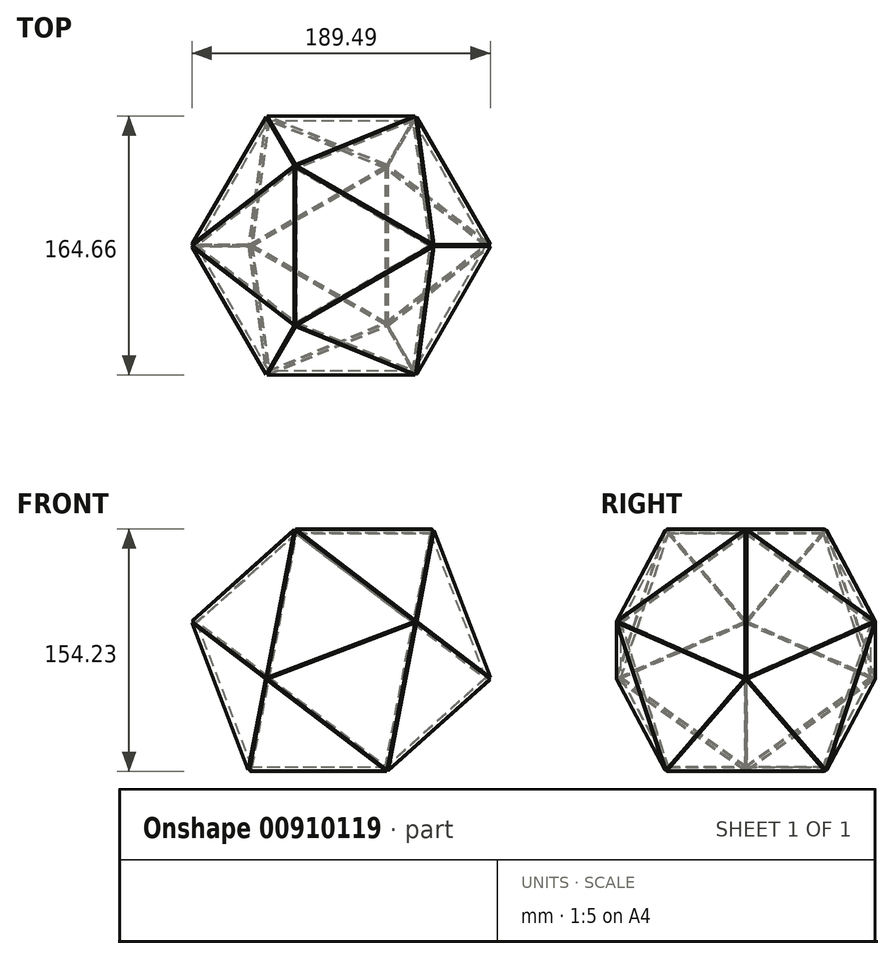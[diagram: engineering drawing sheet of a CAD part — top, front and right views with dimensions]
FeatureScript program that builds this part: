
annotation { "Feature Type Name" : "Feature", "Feature Type Description" : "" }
export const myFeature = defineFeature(function(context is Context, id is Id, definition is map)
    precondition{}
    {
        {
            var Q0;
            Q0=qCreatedBy(makeId("Top.planeOp"),FACE);
            var sketch = newSketch(context, id + "F0", { "sketchPlane" : qUnion([Q0])});
            skCircle(sketch, "E0.cCircle", {"center": v(0, 0) * mm, "radius": 28.87 * mm, "construction": true});
            skLineSegment(sketch, "E0.0", {"start": v(28.87, 50) * mm, "end": v(28.87, -50) * mm});
            skLineSegment(sketch, "E0.1", {"start": v(28.87, -50) * mm, "end": v(-57.74, 0) * mm});
            skLineSegment(sketch, "E0.2", {"start": v(-57.74, 0) * mm, "end": v(28.87, 50) * mm});
            skPoint(sketch, "E0.0.midPoint", {"position": v(28.87, 0) * mm});
            skSolve(sketch);
        }
        {
            var Q0;
            Q0=makeQuery(id+"F0.imprint","IMPRINT",FACE,{"disambiguationData":[TD([[makeQuery(id+"F0.imprint","IMPRINT",EDGE,{"derivedFrom":sQuery(id+"F0.wireOp",EDGE,"E0.0")}),-1.0]])]});
            extrude(context, id + "F1", {"entities" : qUnion([Q0]), "depth" : 3 * mm, "offsetDistance" : 25 * mm});
        }
        {
            var Q0;
            Q0=makeQuery(id+"F1.opExtrude","SWEPT_BODY",BODY,{"disambiguationData":[OSD([sQuery(id+"F0.wireOp",EDGE,"E0.0"),sQuery(id+"F0.wireOp",EDGE,"E0.1"),sQuery(id+"F0.wireOp",EDGE,"E0.2")])]});
            transform(context, id + "F2", {"entities" : qUnion([Q0]), "transformType" : TransformType.TRANSLATION_3D, "dx" : 0 * mm, "dy" : 0 * mm, "dz" : 0 * mm, "makeCopy" : true});
        }
        {
            var Q0;
            Q0=makeQuery(id+"F1.opExtrude","SWEPT_FACE",FACE,{"disambiguationData":[OSD([sQuery(id+"F0.wireOp",EDGE,"E0.1")])]});
            var sketch = newSketch(context, id + "F3", { "sketchPlane" : qUnion([Q0])});
            skLineSegment(sketch, "E1", {"start": v(-50, 1.5) * mm, "end": v(50, 1.5) * mm});
            skSolve(sketch);
        }
        {
            var Q0;
            Q0=makeQuery(id+"F2.opPattern","COPY",BODY,{"derivedFrom":makeQuery(id+"F1.opExtrude","SWEPT_BODY",BODY,{"disambiguationData":[OSD([sQuery(id+"F0.wireOp",EDGE,"E0.0"),sQuery(id+"F0.wireOp",EDGE,"E0.1"),sQuery(id+"F0.wireOp",EDGE,"E0.2")])]}),"instanceName":"1"});
            var Q1;
            Q1=sQuery(id+"F3.wireOp",EDGE,"E1");
            transform(context, id + "F4", {"entities" : qUnion([Q0]), "transformType" : TransformType.ROTATION, "transformAxis" : qUnion([Q1]), "angle" : 138.2 * degree, "makeCopy" : false});
        }
        {
            var Q0;
            Q0=makeQuery(id+"F1.opExtrude","SWEPT_BODY",BODY,{"disambiguationData":[OSD([sQuery(id+"F0.wireOp",EDGE,"E0.0"),sQuery(id+"F0.wireOp",EDGE,"E0.1"),sQuery(id+"F0.wireOp",EDGE,"E0.2")])]});
            transform(context, id + "F5", {"entities" : qUnion([Q0]), "transformType" : TransformType.TRANSLATION_3D, "dx" : 0 * mm, "dy" : 0 * mm, "dz" : 0 * mm, "makeCopy" : true});
        }
        {
            var Q0;
            Q0=makeQuery(id+"F1.opExtrude","SWEPT_FACE",FACE,{"disambiguationData":[OSD([sQuery(id+"F0.wireOp",EDGE,"E0.0")])]});
            var sketch = newSketch(context, id + "F6", { "sketchPlane" : qUnion([Q0])});
            skLineSegment(sketch, "E2", {"start": v(-50, 1.5) * mm, "end": v(50, 1.5) * mm});
            skSolve(sketch);
        }
        {
            var Q0;
            Q0=makeQuery(id+"F5.opPattern","COPY",BODY,{"derivedFrom":makeQuery(id+"F1.opExtrude","SWEPT_BODY",BODY,{"disambiguationData":[OSD([sQuery(id+"F0.wireOp",EDGE,"E0.0"),sQuery(id+"F0.wireOp",EDGE,"E0.1"),sQuery(id+"F0.wireOp",EDGE,"E0.2")])]}),"instanceName":"1"});
            var Q1;
            Q1=sQuery(id+"F6.wireOp",EDGE,"E2");
            transform(context, id + "F7", {"entities" : qUnion([Q0]), "transformType" : TransformType.ROTATION, "transformAxis" : qUnion([Q1]), "angle" : 138.2 * degree, "makeCopy" : false});
        }
        {
            var Q0;
            Q0=makeQuery(id+"F1.opExtrude","SWEPT_BODY",BODY,{"disambiguationData":[OSD([sQuery(id+"F0.wireOp",EDGE,"E0.0"),sQuery(id+"F0.wireOp",EDGE,"E0.1"),sQuery(id+"F0.wireOp",EDGE,"E0.2")])]});
            transform(context, id + "F8", {"entities" : qUnion([Q0]), "transformType" : TransformType.TRANSLATION_3D, "dx" : 0 * mm, "dy" : 0 * mm, "dz" : 0 * mm, "makeCopy" : true});
        }
        {
            var Q0;
            Q0=makeQuery(id+"F1.opExtrude","SWEPT_FACE",FACE,{"disambiguationData":[OSD([sQuery(id+"F0.wireOp",EDGE,"E0.2")])]});
            var sketch = newSketch(context, id + "F9", { "sketchPlane" : qUnion([Q0])});
            skLineSegment(sketch, "E3", {"start": v(-50, 1.5) * mm, "end": v(50, 1.5) * mm});
            skSolve(sketch);
        }
        {
            var Q0;
            Q0=makeQuery(id+"F8.opPattern","COPY",BODY,{"derivedFrom":makeQuery(id+"F1.opExtrude","SWEPT_BODY",BODY,{"disambiguationData":[OSD([sQuery(id+"F0.wireOp",EDGE,"E0.0"),sQuery(id+"F0.wireOp",EDGE,"E0.1"),sQuery(id+"F0.wireOp",EDGE,"E0.2")])]}),"instanceName":"1"});
            var Q1;
            Q1=sQuery(id+"F9.wireOp",EDGE,"E3");
            transform(context, id + "F10", {"entities" : qUnion([Q0]), "transformType" : TransformType.ROTATION, "transformAxis" : qUnion([Q1]), "angle" : 138.2 * degree, "makeCopy" : false});
        }
        {
            var Q0;
            Q0=makeQuery(id+"F2.opPattern","COPY",FACE,{"derivedFrom":makeQuery(id+"F1.opExtrude","SWEPT_FACE",FACE,{"disambiguationData":[OSD([sQuery(id+"F0.wireOp",EDGE,"E0.2")])]}),"instanceName":"1"});
            var sketch = newSketch(context, id + "F11", { "sketchPlane" : qUnion([Q0])});
            skLineSegment(sketch, "E4", {"start": v(87.46, 40.13) * mm, "end": v(6.05, -17.95) * mm});
            skSolve(sketch);
        }
        {
            var Q0;
            Q0=makeQuery(id+"F8.opPattern","COPY",FACE,{"derivedFrom":makeQuery(id+"F1.opExtrude","SWEPT_FACE",FACE,{"disambiguationData":[OSD([sQuery(id+"F0.wireOp",EDGE,"E0.1")])]}),"instanceName":"1"});
            var sketch = newSketch(context, id + "F12", { "sketchPlane" : qUnion([Q0])});
            skLineSegment(sketch, "E5", {"start": v(-87.46, 40.13) * mm, "end": v(-6.05, -17.95) * mm});
            skSolve(sketch);
        }
        {
            var Q0;
            Q0=makeQuery(id+"F2.opPattern","COPY",BODY,{"derivedFrom":makeQuery(id+"F1.opExtrude","SWEPT_BODY",BODY,{"disambiguationData":[OSD([sQuery(id+"F0.wireOp",EDGE,"E0.0"),sQuery(id+"F0.wireOp",EDGE,"E0.1"),sQuery(id+"F0.wireOp",EDGE,"E0.2")])]}),"instanceName":"1"});
            transform(context, id + "F13", {"entities" : qUnion([Q0]), "transformType" : TransformType.TRANSLATION_3D, "dx" : 0 * mm, "dy" : 0 * mm, "dz" : 0 * mm, "makeCopy" : true});
        }
        {
            var Q0;
            Q0=makeQuery(id+"F13.opPattern","COPY",BODY,{"derivedFrom":makeQuery(id+"F2.opPattern","COPY",BODY,{"derivedFrom":makeQuery(id+"F1.opExtrude","SWEPT_BODY",BODY,{"disambiguationData":[OSD([sQuery(id+"F0.wireOp",EDGE,"E0.0"),sQuery(id+"F0.wireOp",EDGE,"E0.1"),sQuery(id+"F0.wireOp",EDGE,"E0.2")])]}),"instanceName":"1"}),"instanceName":"1"});
            var Q1;
            Q1=sQuery(id+"F11.wireOp",EDGE,"E4");
            transform(context, id + "F14", {"entities" : qUnion([Q0]), "transformType" : TransformType.ROTATION, "transformAxis" : qUnion([Q1]), "angle" : 138.2 * degree, "oppositeDirection" : true, "makeCopy" : false});
        }
        {
            var Q0;
            Q0=makeQuery(id+"F8.opPattern","COPY",BODY,{"derivedFrom":makeQuery(id+"F1.opExtrude","SWEPT_BODY",BODY,{"disambiguationData":[OSD([sQuery(id+"F0.wireOp",EDGE,"E0.0"),sQuery(id+"F0.wireOp",EDGE,"E0.1"),sQuery(id+"F0.wireOp",EDGE,"E0.2")])]}),"instanceName":"1"});
            transform(context, id + "F15", {"entities" : qUnion([Q0]), "transformType" : TransformType.TRANSLATION_3D, "dx" : 0 * mm, "dy" : 0 * mm, "dz" : 0 * mm, "makeCopy" : true});
        }
        {
            var Q0;
            Q0=makeQuery(id+"F15.opPattern","COPY",BODY,{"derivedFrom":makeQuery(id+"F8.opPattern","COPY",BODY,{"derivedFrom":makeQuery(id+"F1.opExtrude","SWEPT_BODY",BODY,{"disambiguationData":[OSD([sQuery(id+"F0.wireOp",EDGE,"E0.0"),sQuery(id+"F0.wireOp",EDGE,"E0.1"),sQuery(id+"F0.wireOp",EDGE,"E0.2")])]}),"instanceName":"1"}),"instanceName":"1"});
            var Q1;
            Q1=sQuery(id+"F12.wireOp",EDGE,"E5");
            transform(context, id + "F16", {"entities" : qUnion([Q0]), "transformType" : TransformType.ROTATION, "transformAxis" : qUnion([Q1]), "angle" : 138.2 * degree, "makeCopy" : false});
        }
        {
            var Q0;
            Q0=makeQuery(id+"F8.opPattern","COPY",FACE,{"derivedFrom":makeQuery(id+"F1.opExtrude","SWEPT_FACE",FACE,{"disambiguationData":[OSD([sQuery(id+"F0.wireOp",EDGE,"E0.0")])]}),"instanceName":"1"});
            var sketch = newSketch(context, id + "F17", { "sketchPlane" : qUnion([Q0])});
            skLineSegment(sketch, "E6", {"start": v(2.28, -18.8) * mm, "end": v(93.78, 21.55) * mm});
            skSolve(sketch);
        }
        {
            var Q0;
            Q0=makeQuery(id+"F8.opPattern","COPY",BODY,{"derivedFrom":makeQuery(id+"F1.opExtrude","SWEPT_BODY",BODY,{"disambiguationData":[OSD([sQuery(id+"F0.wireOp",EDGE,"E0.0"),sQuery(id+"F0.wireOp",EDGE,"E0.1"),sQuery(id+"F0.wireOp",EDGE,"E0.2")])]}),"instanceName":"1"});
            transform(context, id + "F18", {"entities" : qUnion([Q0]), "transformType" : TransformType.TRANSLATION_3D, "dx" : 0 * mm, "dy" : 0 * mm, "dz" : 0 * mm, "makeCopy" : true});
        }
        {
            var Q0;
            Q0=makeQuery(id+"F8.opPattern","COPY",BODY,{"derivedFrom":makeQuery(id+"F1.opExtrude","SWEPT_BODY",BODY,{"disambiguationData":[OSD([sQuery(id+"F0.wireOp",EDGE,"E0.0"),sQuery(id+"F0.wireOp",EDGE,"E0.1"),sQuery(id+"F0.wireOp",EDGE,"E0.2")])]}),"instanceName":"1"});
            var Q1;
            Q1=sQuery(id+"F17.wireOp",EDGE,"E6");
            transform(context, id + "F19", {"entities" : qUnion([Q0]), "transformType" : TransformType.ROTATION, "transformAxis" : qUnion([Q1]), "angle" : 138.2 * degree, "makeCopy" : false});
        }
        {
            var Q0;
            Q0=qCreatedBy(makeId("Right.planeOp"),FACE);
            var sketch = newSketch(context, id + "F20", { "sketchPlane" : qUnion([Q0])});
            skLineSegment(sketch, "E7", {"start": v(0, 0) * mm, "end": v(0, 167.31) * mm});
            skSolve(sketch);
        }
        {
            var Q0;
            Q0=makeQuery(id+"F18.opPattern","COPY",BODY,{"derivedFrom":makeQuery(id+"F8.opPattern","COPY",BODY,{"derivedFrom":makeQuery(id+"F1.opExtrude","SWEPT_BODY",BODY,{"disambiguationData":[OSD([sQuery(id+"F0.wireOp",EDGE,"E0.0"),sQuery(id+"F0.wireOp",EDGE,"E0.1"),sQuery(id+"F0.wireOp",EDGE,"E0.2")])]}),"instanceName":"1"}),"instanceName":"1"});
            var Q1;
            Q1=sQuery(id+"F20.wireOp",EDGE,"E7");
            circularPattern(context, id + "F21", {"entities" : qUnion([Q0]), "axis" : qUnion([Q1]), "angle" : 360 * degree, "instanceCount" : 3, "equalSpace" : true});
        }
        {
            var Q0;
            Q0=makeQuery(id+"F15.opPattern","COPY",BODY,{"derivedFrom":makeQuery(id+"F8.opPattern","COPY",BODY,{"derivedFrom":makeQuery(id+"F1.opExtrude","SWEPT_BODY",BODY,{"disambiguationData":[OSD([sQuery(id+"F0.wireOp",EDGE,"E0.0"),sQuery(id+"F0.wireOp",EDGE,"E0.1"),sQuery(id+"F0.wireOp",EDGE,"E0.2")])]}),"instanceName":"1"}),"instanceName":"1"});
            var Q1;
            Q1=sQuery(id+"F20.wireOp",EDGE,"E7");
            circularPattern(context, id + "F22", {"entities" : qUnion([Q0]), "axis" : qUnion([Q1]), "angle" : 360 * degree, "instanceCount" : 3, "equalSpace" : true});
        }
        {
            var Q0;
            Q0=makeQuery(id+"F8.opPattern","COPY",BODY,{"derivedFrom":makeQuery(id+"F1.opExtrude","SWEPT_BODY",BODY,{"disambiguationData":[OSD([sQuery(id+"F0.wireOp",EDGE,"E0.0"),sQuery(id+"F0.wireOp",EDGE,"E0.1"),sQuery(id+"F0.wireOp",EDGE,"E0.2")])]}),"instanceName":"1"});
            var Q1;
            Q1=sQuery(id+"F20.wireOp",EDGE,"E7");
            circularPattern(context, id + "F23", {"entities" : qUnion([Q0]), "axis" : qUnion([Q1]), "angle" : 360 * degree, "instanceCount" : 3, "equalSpace" : true});
        }
        {
            var Q0;
            Q0=makeQuery(id+"F15.opPattern","COPY",FACE,{"derivedFrom":makeQuery(id+"F8.opPattern","COPY",FACE,{"derivedFrom":makeQuery(id+"F1.opExtrude","SWEPT_FACE",FACE,{"disambiguationData":[OSD([sQuery(id+"F0.wireOp",EDGE,"E0.0")])]}),"instanceName":"1"}),"instanceName":"1"});
            var sketch = newSketch(context, id + "F24", { "sketchPlane" : qUnion([Q0])});
            skLineSegment(sketch, "E8", {"start": v(-80.56, -44.79) * mm, "end": v(-33.35, 43.37) * mm});
            skSolve(sketch);
        }
        {
            var Q0;
            Q0=makeQuery(id+"F15.opPattern","COPY",BODY,{"derivedFrom":makeQuery(id+"F8.opPattern","COPY",BODY,{"derivedFrom":makeQuery(id+"F1.opExtrude","SWEPT_BODY",BODY,{"disambiguationData":[OSD([sQuery(id+"F0.wireOp",EDGE,"E0.0"),sQuery(id+"F0.wireOp",EDGE,"E0.1"),sQuery(id+"F0.wireOp",EDGE,"E0.2")])]}),"instanceName":"1"}),"instanceName":"1"});
            transform(context, id + "F25", {"entities" : qUnion([Q0]), "transformType" : TransformType.TRANSLATION_3D, "dx" : 0 * mm, "dy" : 0 * mm, "dz" : 0 * mm, "makeCopy" : true});
        }
        {
            var Q0;
            Q0=makeQuery(id+"F25.opPattern","COPY",BODY,{"derivedFrom":makeQuery(id+"F15.opPattern","COPY",BODY,{"derivedFrom":makeQuery(id+"F8.opPattern","COPY",BODY,{"derivedFrom":makeQuery(id+"F1.opExtrude","SWEPT_BODY",BODY,{"disambiguationData":[OSD([sQuery(id+"F0.wireOp",EDGE,"E0.0"),sQuery(id+"F0.wireOp",EDGE,"E0.1"),sQuery(id+"F0.wireOp",EDGE,"E0.2")])]}),"instanceName":"1"}),"instanceName":"1"}),"instanceName":"1"});
            var Q1;
            Q1=sQuery(id+"F24.wireOp",EDGE,"E8");
            transform(context, id + "F26", {"entities" : qUnion([Q0]), "transformType" : TransformType.ROTATION, "transformAxis" : qUnion([Q1]), "angle" : 138.2 * degree, "oppositeDirection" : true, "makeCopy" : false});
        }
        {
            var Q0;
            Q0=makeQuery(id+"F25.opPattern","COPY",BODY,{"derivedFrom":makeQuery(id+"F15.opPattern","COPY",BODY,{"derivedFrom":makeQuery(id+"F8.opPattern","COPY",BODY,{"derivedFrom":makeQuery(id+"F1.opExtrude","SWEPT_BODY",BODY,{"disambiguationData":[OSD([sQuery(id+"F0.wireOp",EDGE,"E0.0"),sQuery(id+"F0.wireOp",EDGE,"E0.1"),sQuery(id+"F0.wireOp",EDGE,"E0.2")])]}),"instanceName":"1"}),"instanceName":"1"}),"instanceName":"1"});
            var Q1;
            Q1=sQuery(id+"F20.wireOp",EDGE,"E7");
            circularPattern(context, id + "F27", {"entities" : qUnion([Q0]), "axis" : qUnion([Q1]), "angle" : 360 * degree, "instanceCount" : 3, "equalSpace" : true});
        }
        {
            var Q0;
            Q0=makeQuery(id+"F13.opPattern","COPY",BODY,{"derivedFrom":makeQuery(id+"F2.opPattern","COPY",BODY,{"derivedFrom":makeQuery(id+"F1.opExtrude","SWEPT_BODY",BODY,{"disambiguationData":[OSD([sQuery(id+"F0.wireOp",EDGE,"E0.0"),sQuery(id+"F0.wireOp",EDGE,"E0.1"),sQuery(id+"F0.wireOp",EDGE,"E0.2")])]}),"instanceName":"1"}),"instanceName":"1"});
            transform(context, id + "F28", {"entities" : qUnion([Q0]), "transformType" : TransformType.TRANSLATION_3D, "dx" : 0 * mm, "dy" : 0 * mm, "dz" : 0 * mm, "makeCopy" : true});
        }
        {
            var Q0;
            Q0=makeQuery(id+"F13.opPattern","COPY",FACE,{"derivedFrom":makeQuery(id+"F2.opPattern","COPY",FACE,{"derivedFrom":makeQuery(id+"F1.opExtrude","SWEPT_FACE",FACE,{"disambiguationData":[OSD([sQuery(id+"F0.wireOp",EDGE,"E0.0")])]}),"instanceName":"1"}),"instanceName":"1"});
            var sketch = newSketch(context, id + "F29", { "sketchPlane" : qUnion([Q0])});
            skLineSegment(sketch, "E9", {"start": v(-80.56, 44.79) * mm, "end": v(-33.35, -43.37) * mm});
            skSolve(sketch);
        }
        {
            var Q0;
            Q0=makeQuery(id+"F28.opPattern","COPY",BODY,{"derivedFrom":makeQuery(id+"F13.opPattern","COPY",BODY,{"derivedFrom":makeQuery(id+"F2.opPattern","COPY",BODY,{"derivedFrom":makeQuery(id+"F1.opExtrude","SWEPT_BODY",BODY,{"disambiguationData":[OSD([sQuery(id+"F0.wireOp",EDGE,"E0.0"),sQuery(id+"F0.wireOp",EDGE,"E0.1"),sQuery(id+"F0.wireOp",EDGE,"E0.2")])]}),"instanceName":"1"}),"instanceName":"1"}),"instanceName":"1"});
            var Q1;
            Q1=sQuery(id+"F29.wireOp",EDGE,"E9");
            transform(context, id + "F30", {"entities" : qUnion([Q0]), "transformType" : TransformType.ROTATION, "transformAxis" : qUnion([Q1]), "angle" : 138.2 * degree, "makeCopy" : false});
        }
        {
            var Q0;
            Q0=makeQuery(id+"F28.opPattern","COPY",BODY,{"derivedFrom":makeQuery(id+"F13.opPattern","COPY",BODY,{"derivedFrom":makeQuery(id+"F2.opPattern","COPY",BODY,{"derivedFrom":makeQuery(id+"F1.opExtrude","SWEPT_BODY",BODY,{"disambiguationData":[OSD([sQuery(id+"F0.wireOp",EDGE,"E0.0"),sQuery(id+"F0.wireOp",EDGE,"E0.1"),sQuery(id+"F0.wireOp",EDGE,"E0.2")])]}),"instanceName":"1"}),"instanceName":"1"}),"instanceName":"1"});
            var Q1;
            Q1=sQuery(id+"F20.wireOp",EDGE,"E7");
            circularPattern(context, id + "F31", {"entities" : qUnion([Q0]), "axis" : qUnion([Q1]), "angle" : 360 * degree, "instanceCount" : 3, "equalSpace" : true});
        }
        {
            var Q0;
            Q0=makeQuery(id+"F28.opPattern","COPY",BODY,{"derivedFrom":makeQuery(id+"F13.opPattern","COPY",BODY,{"derivedFrom":makeQuery(id+"F2.opPattern","COPY",BODY,{"derivedFrom":makeQuery(id+"F1.opExtrude","SWEPT_BODY",BODY,{"disambiguationData":[OSD([sQuery(id+"F0.wireOp",EDGE,"E0.0"),sQuery(id+"F0.wireOp",EDGE,"E0.1"),sQuery(id+"F0.wireOp",EDGE,"E0.2")])]}),"instanceName":"1"}),"instanceName":"1"}),"instanceName":"1"});
            transform(context, id + "F32", {"entities" : qUnion([Q0]), "transformType" : TransformType.TRANSLATION_3D, "dx" : 0 * mm, "dy" : 0 * mm, "dz" : 0 * mm, "makeCopy" : true});
        }
        {
            var Q0;
            Q0=makeQuery(id+"F28.opPattern","COPY",FACE,{"derivedFrom":makeQuery(id+"F13.opPattern","COPY",FACE,{"derivedFrom":makeQuery(id+"F2.opPattern","COPY",FACE,{"derivedFrom":makeQuery(id+"F1.opExtrude","SWEPT_FACE",FACE,{"disambiguationData":[OSD([sQuery(id+"F0.wireOp",EDGE,"E0.1")])]}),"instanceName":"1"}),"instanceName":"1"}),"instanceName":"1"});
            var sketch = newSketch(context, id + "F33", { "sketchPlane" : qUnion([Q0])});
            skLineSegment(sketch, "E10", {"start": v(-14.7, -137.74) * mm, "end": v(-80.15, -62.13) * mm});
            skSolve(sketch);
        }
        {
            var Q0;
            Q0=makeQuery(id+"F28.opPattern","COPY",BODY,{"derivedFrom":makeQuery(id+"F13.opPattern","COPY",BODY,{"derivedFrom":makeQuery(id+"F2.opPattern","COPY",BODY,{"derivedFrom":makeQuery(id+"F1.opExtrude","SWEPT_BODY",BODY,{"disambiguationData":[OSD([sQuery(id+"F0.wireOp",EDGE,"E0.0"),sQuery(id+"F0.wireOp",EDGE,"E0.1"),sQuery(id+"F0.wireOp",EDGE,"E0.2")])]}),"instanceName":"1"}),"instanceName":"1"}),"instanceName":"1"});
            var Q1;
            Q1=sQuery(id+"F33.wireOp",EDGE,"E10");
            var Q2;
            Q2=sQuery(id+"F33.wireOp",EDGE,"E10");
            transform(context, id + "F34", {"entities" : qUnion([Q0]), "transformType" : TransformType.ROTATION, "transformAxis" : qUnion([Q2]), "angle" : 138.2 * degree, "oppositeDirection" : true, "makeCopy" : false});
        }
        {
            var Q0;
            Q0=makeQuery(id+"F28.opPattern","COPY",BODY,{"derivedFrom":makeQuery(id+"F13.opPattern","COPY",BODY,{"derivedFrom":makeQuery(id+"F2.opPattern","COPY",BODY,{"derivedFrom":makeQuery(id+"F1.opExtrude","SWEPT_BODY",BODY,{"disambiguationData":[OSD([sQuery(id+"F0.wireOp",EDGE,"E0.0"),sQuery(id+"F0.wireOp",EDGE,"E0.1"),sQuery(id+"F0.wireOp",EDGE,"E0.2")])]}),"instanceName":"1"}),"instanceName":"1"}),"instanceName":"1"});
            var Q1;
            Q1=sQuery(id+"F20.wireOp",EDGE,"E7");
            circularPattern(context, id + "F35", {"entities" : qUnion([Q0]), "axis" : qUnion([Q1]), "angle" : 360 * degree, "instanceCount" : 3, "equalSpace" : true});
        }
        {
            var Q0;
            Q0=makeQuery(id+"F28.opPattern","COPY",BODY,{"derivedFrom":makeQuery(id+"F13.opPattern","COPY",BODY,{"derivedFrom":makeQuery(id+"F2.opPattern","COPY",BODY,{"derivedFrom":makeQuery(id+"F1.opExtrude","SWEPT_BODY",BODY,{"disambiguationData":[OSD([sQuery(id+"F0.wireOp",EDGE,"E0.0"),sQuery(id+"F0.wireOp",EDGE,"E0.1"),sQuery(id+"F0.wireOp",EDGE,"E0.2")])]}),"instanceName":"1"}),"instanceName":"1"}),"instanceName":"1"});
            transform(context, id + "F36", {"entities" : qUnion([Q0]), "transformType" : TransformType.TRANSLATION_3D, "dx" : 0 * mm, "dy" : 0 * mm, "dz" : 0 * mm, "makeCopy" : true});
        }
        {
            var Q0;
            Q0=makeQuery(id+"F28.opPattern","COPY",BODY,{"derivedFrom":makeQuery(id+"F13.opPattern","COPY",BODY,{"derivedFrom":makeQuery(id+"F2.opPattern","COPY",BODY,{"derivedFrom":makeQuery(id+"F1.opExtrude","SWEPT_BODY",BODY,{"disambiguationData":[OSD([sQuery(id+"F0.wireOp",EDGE,"E0.0"),sQuery(id+"F0.wireOp",EDGE,"E0.1"),sQuery(id+"F0.wireOp",EDGE,"E0.2")])]}),"instanceName":"1"}),"instanceName":"1"}),"instanceName":"1"});
            transform(context, id + "F37", {"entities" : qUnion([Q0]), "transformType" : TransformType.TRANSLATION_3D, "dx" : 0 * mm, "dy" : 0 * mm, "dz" : 0 * mm, "makeCopy" : true});
        }
        {
            var Q0;
            Q0=makeQuery(id+"F28.opPattern","COPY",FACE,{"derivedFrom":makeQuery(id+"F13.opPattern","COPY",FACE,{"derivedFrom":makeQuery(id+"F2.opPattern","COPY",FACE,{"derivedFrom":makeQuery(id+"F1.opExtrude","SWEPT_FACE",FACE,{"disambiguationData":[OSD([sQuery(id+"F0.wireOp",EDGE,"E0.2")])]}),"instanceName":"1"}),"instanceName":"1"}),"instanceName":"1"});
            var sketch = newSketch(context, id + "F38", { "sketchPlane" : qUnion([Q0])});
            skLineSegment(sketch, "E11", {"start": v(-50.02, 133.02) * mm, "end": v(49.98, 133.06) * mm});
            skSolve(sketch);
        }
        {
            var Q0;
            Q0=makeQuery(id+"F28.opPattern","COPY",BODY,{"derivedFrom":makeQuery(id+"F13.opPattern","COPY",BODY,{"derivedFrom":makeQuery(id+"F2.opPattern","COPY",BODY,{"derivedFrom":makeQuery(id+"F1.opExtrude","SWEPT_BODY",BODY,{"disambiguationData":[OSD([sQuery(id+"F0.wireOp",EDGE,"E0.0"),sQuery(id+"F0.wireOp",EDGE,"E0.1"),sQuery(id+"F0.wireOp",EDGE,"E0.2")])]}),"instanceName":"1"}),"instanceName":"1"}),"instanceName":"1"});
            var Q1;
            Q1=makeQuery(id+"F37.opPattern","COPY",BODY,{"derivedFrom":makeQuery(id+"F28.opPattern","COPY",BODY,{"derivedFrom":makeQuery(id+"F13.opPattern","COPY",BODY,{"derivedFrom":makeQuery(id+"F2.opPattern","COPY",BODY,{"derivedFrom":makeQuery(id+"F1.opExtrude","SWEPT_BODY",BODY,{"disambiguationData":[OSD([sQuery(id+"F0.wireOp",EDGE,"E0.0"),sQuery(id+"F0.wireOp",EDGE,"E0.1"),sQuery(id+"F0.wireOp",EDGE,"E0.2")])]}),"instanceName":"1"}),"instanceName":"1"}),"instanceName":"1"}),"instanceName":"1"});
            var Q2;
            Q2=sQuery(id+"F38.wireOp",EDGE,"E11");
            transform(context, id + "F39", {"entities" : qUnion([Q0, Q1]), "transformType" : TransformType.ROTATION, "transformAxis" : qUnion([Q2]), "angle" : 138.2 * degree, "oppositeDirection" : true, "makeCopy" : false});
        }
    });
